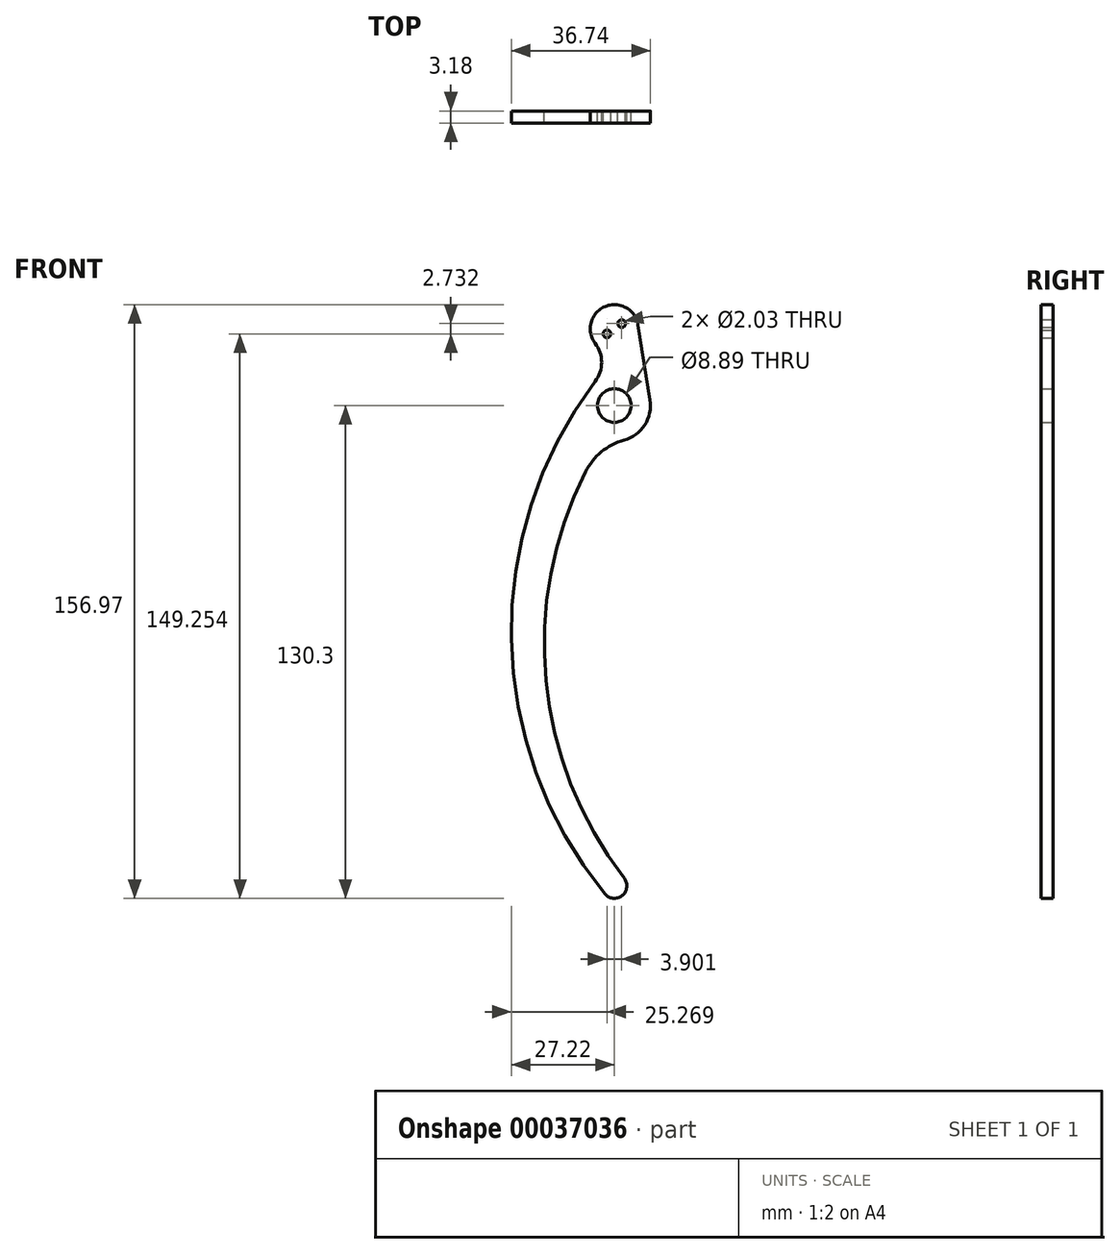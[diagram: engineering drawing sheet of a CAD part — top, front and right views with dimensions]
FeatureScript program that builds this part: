
annotation { "Feature Type Name" : "Feature", "Feature Type Description" : "" }
export const myFeature = defineFeature(function(context is Context, id is Id, definition is map)
    precondition{}
    {
        {
            var Q0;
            Q0=qCreatedBy(makeId("Front.planeOp"),FACE);
            var sketch = newSketch(context, id + "F0", { "sketchPlane" : qUnion([Q0])});
            skLineSegment(sketch, "E0", {"start": v(0, 0) * mm, "end": v(0, -127) * mm, "construction": true});
            skLineSegment(sketch, "E1", {"start": v(0, 0) * mm, "end": v(0, 20.32) * mm, "construction": true});
            skArc(sketch, "E2", {"start": v(6.27, 21.31) * mm, "mid": v(-2.48, 26.16) * mm, "end": v(-5.07, 16.5) * mm});
            skLineSegment(sketch, "E3", {"start": v(6.27, 21.31) * mm, "end": v(9.4, 1.49) * mm});
            skArc(sketch, "E4", {"start": v(9.4, 1.49) * mm, "mid": v(8, -5.16) * mm, "end": v(2.54, -9.18) * mm});
            skArc(sketch, "E5", {"start": v(-2.56, -129.09) * mm, "mid": v(2.05, -129.59) * mm, "end": v(2.61, -124.98) * mm});
            skArc(sketch, "E6", {"start": v(-2.56, -129.09) * mm, "mid": v(-27.2, -61.8) * mm, "end": v(-5.07, 6.36) * mm});
            skArc(sketch, "E7", {"start": v(-5.07, 16.5) * mm, "mid": v(-3.37, 11.43) * mm, "end": v(-5.07, 6.36) * mm});
            skLineSegment(sketch, "E8", {"start": v(-9.53, 0) * mm, "end": v(9.53, 0) * mm, "construction": true});
            skCircle(sketch, "E9", {"center": v(0, 0) * mm, "radius": 4.45 * mm});
            skArc(sketch, "E10", {"start": v(2.54, -9.18) * mm, "mid": v(-3.42, -12.27) * mm, "end": v(-7.62, -17.5) * mm});
            skArc(sketch, "E11", {"start": v(-7.62, -17.5) * mm, "mid": v(-18.06, -72.72) * mm, "end": v(2.61, -124.98) * mm});
            skLineSegment(sketch, "E12", {"start": v(-1.95, 18.95) * mm, "end": v(1.95, 21.69) * mm, "construction": true});
            skCircle(sketch, "E13", {"center": v(-1.95, 18.95) * mm, "radius": 1.02 * mm});
            skCircle(sketch, "E14", {"center": v(1.95, 21.69) * mm, "radius": 1.02 * mm});
            skSolve(sketch);
        }
        {
            var Q0;
            Q0=qSketchRegion(id+"F0",true);
            extrude(context, id + "F1", {"entities" : qUnion([Q0]), "depth" : 3.17 * mm});
        }
    });
